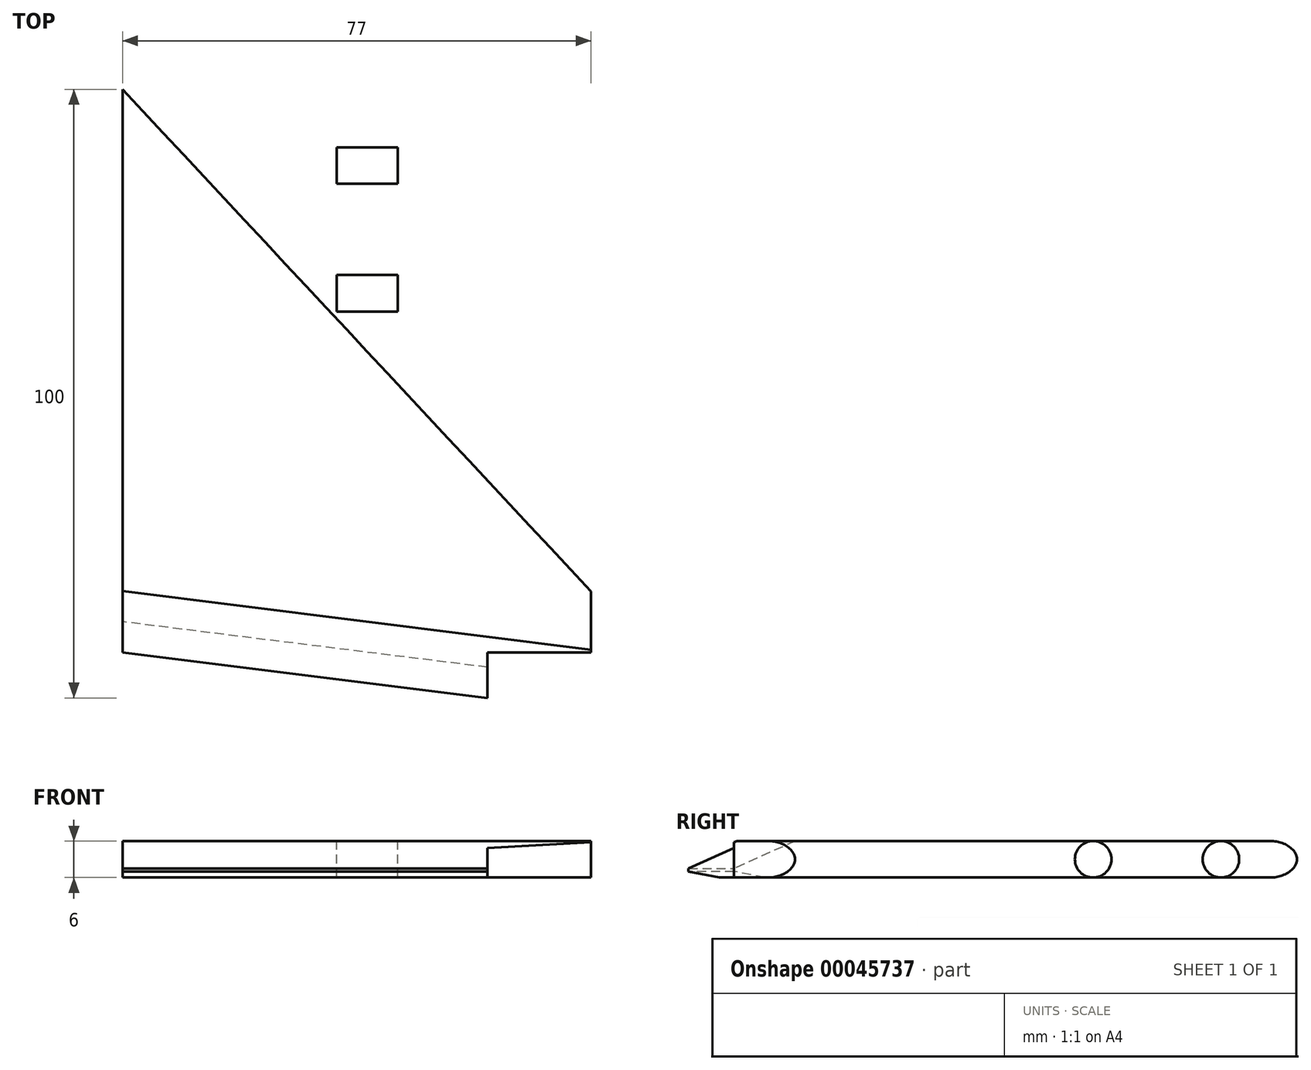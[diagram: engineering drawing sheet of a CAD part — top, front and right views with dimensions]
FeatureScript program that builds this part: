
annotation { "Feature Type Name" : "Feature", "Feature Type Description" : "" }
export const myFeature = defineFeature(function(context is Context, id is Id, definition is map)
    precondition{}
    {
        {
            var Q0;
            Q0=qCreatedBy(makeId("Top.planeOp"),FACE);
            var sketch = newSketch(context, id + "F0", { "sketchPlane" : qUnion([Q0])});
            skLineSegment(sketch, "E0", {"start": v(-35.2, 17.38) * mm, "end": v(-35.2, -57.62) * mm});
            skLineSegment(sketch, "E1", {"start": v(-35.2, -57.62) * mm, "end": v(34.8, -57.62) * mm});
            skLineSegment(sketch, "E2", {"start": v(-35.2, 17.38) * mm, "end": v(34.8, -57.62) * mm});
            skLineSegment(sketch, "E3", {"start": v(-35.2, -57.62) * mm, "end": v(-35.2, -67.62) * mm});
            skLineSegment(sketch, "E4", {"start": v(-35.2, -67.62) * mm, "end": v(34.8, -67.62) * mm});
            skLineSegment(sketch, "E5", {"start": v(34.8, -67.62) * mm, "end": v(24.8, -67.62) * mm});
            skLineSegment(sketch, "E6", {"start": v(24.8, -67.62) * mm, "end": v(24.8, -75.12) * mm});
            skLineSegment(sketch, "E7", {"start": v(24.8, -75.12) * mm, "end": v(-35.2, -67.62) * mm});
            skLineSegment(sketch, "E8", {"start": v(-35.2, 17.38) * mm, "end": v(-35.2, 24.88) * mm});
            skLineSegment(sketch, "E9", {"start": v(34.8, -57.62) * mm, "end": v(41.8, -57.62) * mm});
            skLineSegment(sketch, "E10", {"start": v(34.8, -67.62) * mm, "end": v(41.8, -67.62) * mm});
            skLineSegment(sketch, "E11", {"start": v(41.8, -57.62) * mm, "end": v(41.8, -67.62) * mm});
            skLineSegment(sketch, "E12", {"start": v(-35.2, 24.88) * mm, "end": v(41.8, -57.62) * mm});
            skLineSegment(sketch, "E13", {"start": v(41.8, -67.62) * mm, "end": v(24.8, -75.12) * mm});
            skSolve(sketch);
        }
        {
            var Q0;
            Q0=makeQuery(id+"F0.imprint","IMPRINT",FACE,{"disambiguationData":[TD([[makeQuery(id+"F0.imprint","IMPRINT",EDGE,{"derivedFrom":sQuery(id+"F0.wireOp",EDGE,"E5")}),1.0]])]});
            var Q1;
            Q1=makeQuery(id+"F0.imprint","IMPRINT",FACE,{"disambiguationData":[TD([[makeQuery(id+"F0.imprint","IMPRINT",EDGE,{"derivedFrom":sQuery(id+"F0.wireOp",EDGE,"E1")}),-1.0]])]});
            var Q2;
            Q2=makeQuery(id+"F0.imprint","IMPRINT",FACE,{"disambiguationData":[TD([[makeQuery(id+"F0.imprint","IMPRINT",EDGE,{"derivedFrom":sQuery(id+"F0.wireOp",EDGE,"E4")}),-1.0]])]});
            var Q3;
            Q3=makeQuery(id+"F0.imprint","IMPRINT",FACE,{"disambiguationData":[TD([[makeQuery(id+"F0.imprint","IMPRINT",EDGE,{"derivedFrom":sQuery(id+"F0.wireOp",EDGE,"E0")}),1.0]])]});
            extrude(context, id + "F1", {"entities" : qUnion([Q0, Q1, Q2, Q3]), "depth" : 6 * mm});
        }
        {
            var Q0;
            Q0=makeQuery(id+"F0.imprint","IMPRINT",FACE,{"disambiguationData":[TD([[makeQuery(id+"F0.imprint","IMPRINT",EDGE,{"derivedFrom":sQuery(id+"F0.wireOp",EDGE,"E2")}),1.0]])]});
            extrude(context, id + "F2", {"entities" : qUnion([Q0]), "operationType" : NewBodyOperationType.ADD, "depth" : 6 * mm});
        }
        {
            var Q0;
            Q0=makeQuery(id+"F2.opExtrude","CAP_EDGE",EDGE,{"disambiguationData":[OSD([sQuery(id+"F0.wireOp",EDGE,"E12")])],"isStart":false});
            var Q1;
            Q1=makeQuery(id+"F2.opExtrude","CAP_EDGE",EDGE,{"disambiguationData":[OSD([sQuery(id+"F0.wireOp",EDGE,"E12")])],"isStart":true});
            fillet(context, id + "F3", {"entities" : qUnion([Q0, Q1]), "radius" : 3 * mm, "tangentPropagation" : true, "rho" : .4, "crossSection" : FilletCrossSection.CONIC, "allowEdgeOverflow" : false});
        }
        {
            var Q0;
            Q0=makeQuery(id+"F1.opExtrude","CAP_EDGE",EDGE,{"disambiguationData":[OSD([sQuery(id+"F0.wireOp",EDGE,"E7")])],"isStart":false});
            var Q1;
            Q1=makeQuery(id+"F1.opExtrude","CAP_EDGE",EDGE,{"disambiguationData":[OSD([sQuery(id+"F0.wireOp",EDGE,"E13")])],"isStart":false});
            chamfer(context, id + "F4", {"entities" : qUnion([Q0, Q1]), "chamferType" : ChamferType.TWO_OFFSETS, "width1" : 4.5 * mm, "oppositeDirection" : false, "width2" : 10 * mm, "tangentPropagation" : true});
        }
        {
            var Q0;
            Q0=makeQuery(id+"F1.opExtrude","CAP_EDGE",EDGE,{"disambiguationData":[OSD([sQuery(id+"F0.wireOp",EDGE,"E13")])],"isStart":true});
            var Q1;
            Q1=makeQuery(id+"F1.opExtrude","CAP_EDGE",EDGE,{"disambiguationData":[OSD([sQuery(id+"F0.wireOp",EDGE,"E7")])],"isStart":true});
            chamfer(context, id + "F5", {"entities" : qUnion([Q0, Q1]), "chamferType" : ChamferType.TWO_OFFSETS, "width1" : 5 * mm, "oppositeDirection" : false, "width2" : 1 * mm, "tangentPropagation" : true});
        }
        {
            var Q0;
            Q0=qCreatedBy(makeId("Right.planeOp"),FACE);
            var sketch = newSketch(context, id + "F6", { "sketchPlane" : qUnion([Q0])});
            skCircle(sketch, "E14", {"center": v(12.38, 3) * mm, "radius": 3 * mm});
            skCircle(sketch, "E15", {"center": v(-8.62, 3) * mm, "radius": 3 * mm});
            skSolve(sketch);
        }
        {
            var Q0;
            Q0=makeQuery(id+"F6.imprint","IMPRINT",FACE,{"disambiguationData":[TD([[makeQuery(id+"F6.imprint","IMPRINT",EDGE,{"derivedFrom":sQuery(id+"F6.wireOp",EDGE,"E14")}),1.0]])]});
            var Q1;
            Q1=makeQuery(id+"F6.imprint","IMPRINT",FACE,{"disambiguationData":[TD([[makeQuery(id+"F6.imprint","IMPRINT",EDGE,{"derivedFrom":sQuery(id+"F6.wireOp",EDGE,"E15")}),1.0]])]});
            extrude(context, id + "F7", {"entities" : qUnion([Q0, Q1]), "depth" : 10 * mm});
        }
    });
